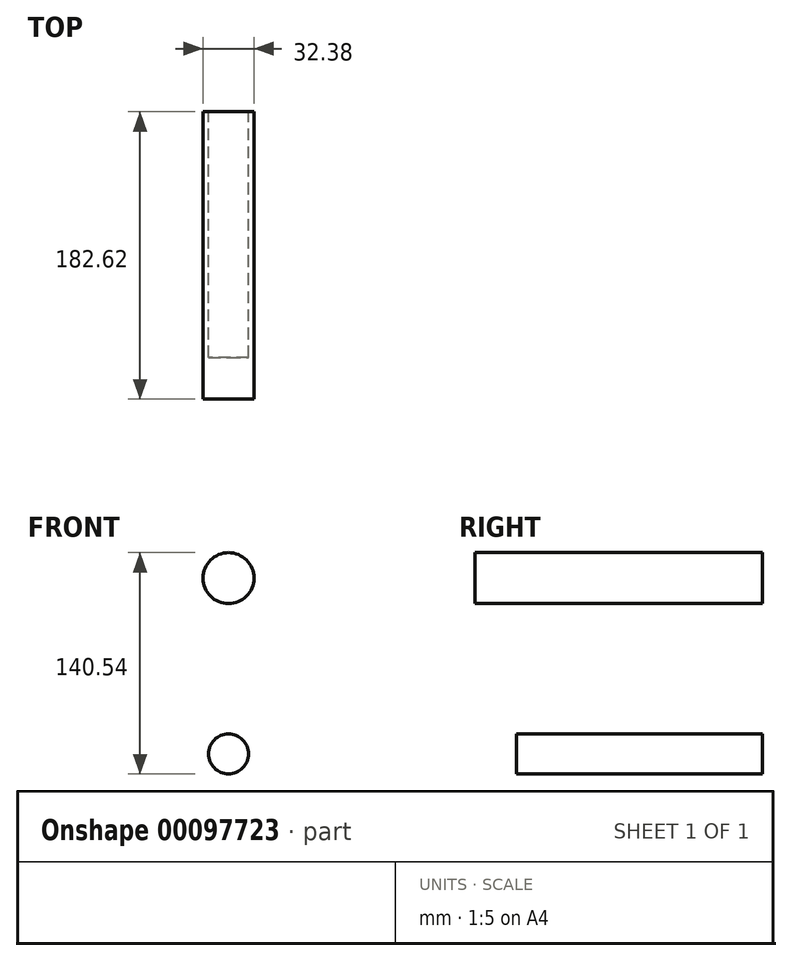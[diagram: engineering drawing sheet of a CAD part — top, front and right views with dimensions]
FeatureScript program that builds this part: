
annotation { "Feature Type Name" : "Feature", "Feature Type Description" : "" }
export const myFeature = defineFeature(function(context is Context, id is Id, definition is map)
    precondition{}
    {
        {
            var Q0;
            Q0=qCreatedBy(makeId("Front.planeOp"),FACE);
            var sketch = newSketch(context, id + "F0", { "sketchPlane" : qUnion([Q0])});
            skCircle(sketch, "E0", {"center": v(0, 0) * mm, "radius": 12.7 * mm});
            skSolve(sketch);
        }
        {
            var Q0;
            Q0 = qSketchRegion(id + "F0", true);
            extrude(context, id + "F1", {"entities" : qUnion([Q0]), "depth" : 156.1 * mm});
        }
        {
            var Q0;
            Q0=qCreatedBy(makeId("Top.planeOp"),FACE);
            var sketch = newSketch(context, id + "F2", { "sketchPlane" : qUnion([Q0])});
            skCircle(sketch, "E1", {"center": v(0, -30.22) * mm, "radius": 8.9 * mm});
            skCircle(sketch, "E2", {"center": v(0, -132.27) * mm, "radius": 11.47 * mm});
            skSolve(sketch);
        }
        {
            var Q0;
            Q0=sQuery(id+"F2.wireOp",EDGE,"E2");
            extrude(context, id + "F3", {"bodyType" : ToolBodyType.SURFACE, "surfaceEntities" : qUnion([Q0]), "depth" : 100.3 * mm});
        }
        {
            var Q0;
            Q0=qCreatedBy(makeId("Front.planeOp"),FACE);
            var sketch = newSketch(context, id + "F4", { "sketchPlane" : qUnion([Q0])});
            skCircle(sketch, "E3", {"center": v(0, 111.65) * mm, "radius": 16.19 * mm});
            skSolve(sketch);
        }
        {
            var Q0;
            Q0 = qSketchRegion(id + "F4", true);
            extrude(context, id + "F5", {"entities" : qUnion([Q0]), "operationType" : NewBodyOperationType.ADD, "depth" : 182.62 * mm});
        }
        {
            var Q0;
            Q0=qCreatedBy(makeId("Front.planeOp"),FACE);
            var sketch = newSketch(context, id + "F6", { "sketchPlane" : qUnion([Q0])});
            skCircle(sketch, "E4", {"center": v(0, 0) * mm, "radius": 9.6 * mm});
            skSolve(sketch);
        }
        {
            var Q0;
            Q0=sQuery(id+"F6.wireOp",EDGE,"E4");
            extrude(context, id + "F7", {"bodyType" : ToolBodyType.SURFACE, "surfaceEntities" : qUnion([Q0]), "depth" : 317.27 * mm});
        }
    });
